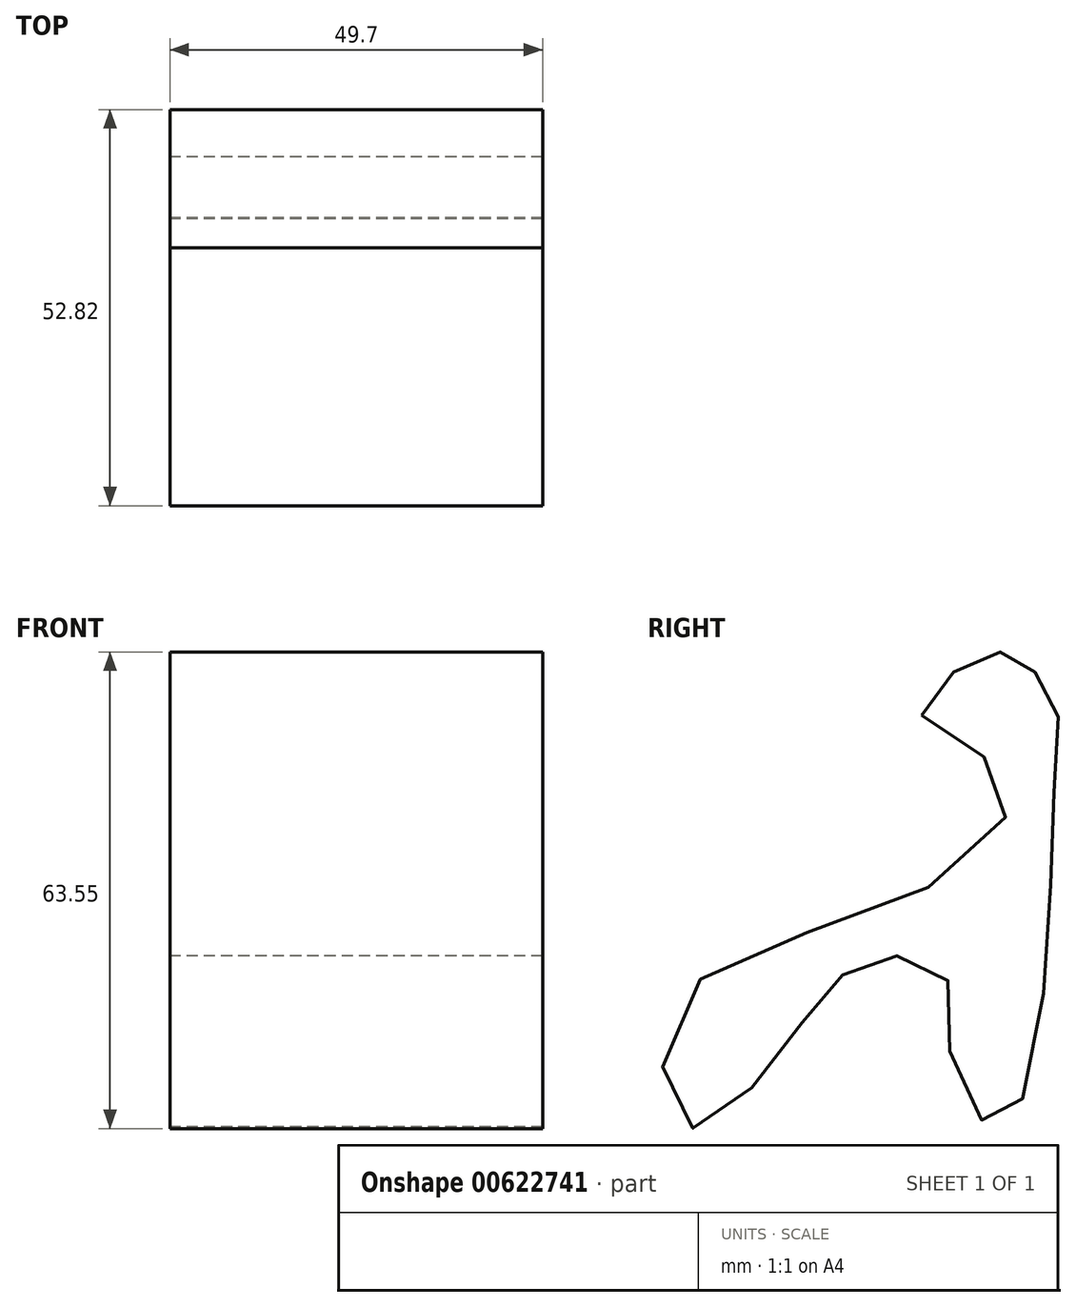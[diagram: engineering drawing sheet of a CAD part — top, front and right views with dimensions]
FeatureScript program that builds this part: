
annotation { "Feature Type Name" : "Feature", "Feature Type Description" : "" }
export const myFeature = defineFeature(function(context is Context, id is Id, definition is map)
    precondition{}
    {
        {
            var Q0;
            Q0=qCreatedBy(makeId("Right.planeOp"),FACE);
            var sketch = newSketch(context, id + "F0", { "sketchPlane" : qUnion([Q0])});
            skFitSpline(sketch, "E0", {"points": [v(38.68, 54.85) * mm, v(43.16, 60.82) * mm, v(49.12, 63.3) * mm, v(52.6, 61.56) * mm, v(56.34, 57.33) * mm, v(56.34, 44.65) * mm, v(55.1, 19.28) * mm, v(49.12, 0) * mm, v(42.66, 8.33) * mm, v(41.66, 20.52) * mm, v(32.7, 22.51) * mm, v(26.24, 18.28) * mm, v(17.78, 7.34) * mm, v(7.34, 0) * mm, v(6.1, 16.3) * mm, v(38.18, 31.22) * mm, v(50.12, 46.39) * mm, v(38.68, 54.85) * mm]});
            skSolve(sketch);
        }
        {
            var Q0;
            Q0 = qSketchRegion(id + "F0", true);
            extrude(context, id + "F1", {"entities" : qUnion([Q0]), "depth" : 49.7 * mm, "offsetDistance" : 25 * mm});
        }
    });
